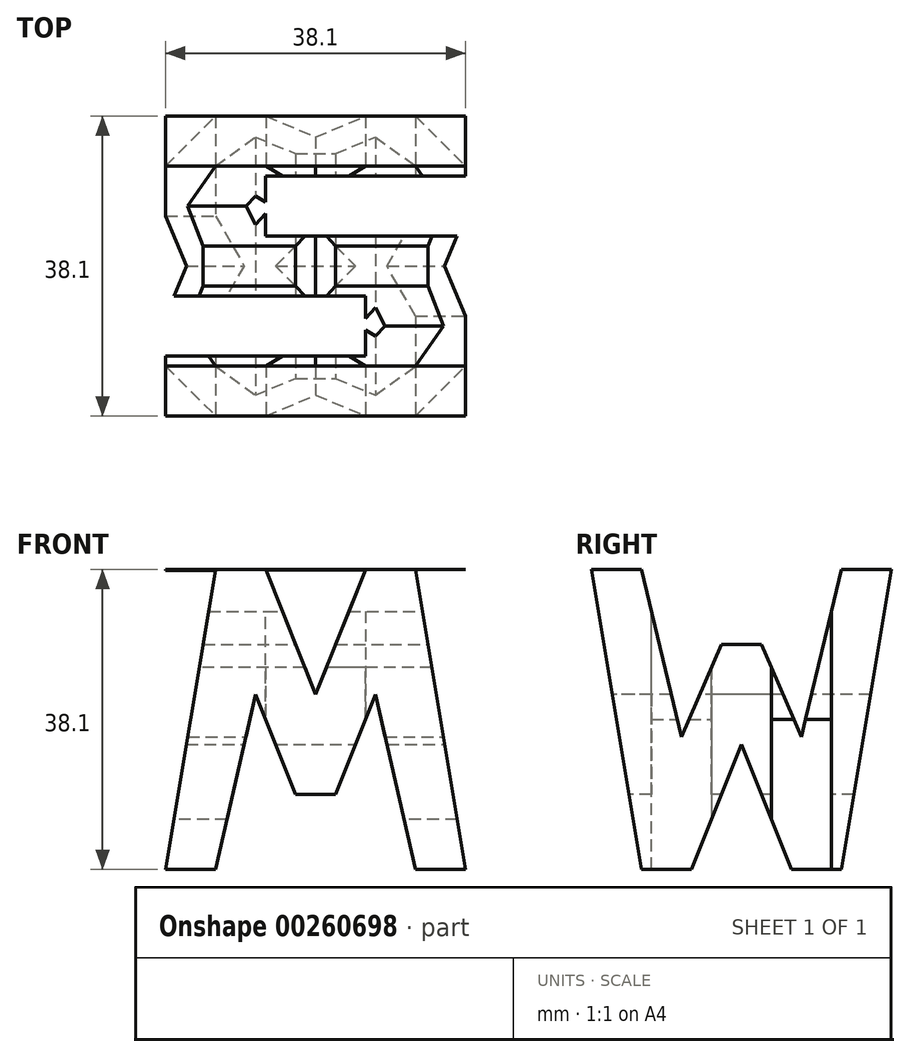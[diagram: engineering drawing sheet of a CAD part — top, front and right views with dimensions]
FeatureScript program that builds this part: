
annotation { "Feature Type Name" : "Feature", "Feature Type Description" : "" }
export const myFeature = defineFeature(function(context is Context, id is Id, definition is map)
    precondition{}
    {
        {
            var Q0;
            Q0=qCreatedBy(makeId("Front.planeOp"),FACE);
            var sketch = newSketch(context, id + "F0", { "sketchPlane" : qUnion([Q0])});
            skLineSegment(sketch, "E0", {"start": v(0, 0) * mm, "end": v(0, 38.1) * mm});
            skLineSegment(sketch, "E1", {"start": v(0, 38.1) * mm, "end": v(38.1, 38.1) * mm});
            skLineSegment(sketch, "E2", {"start": v(38.1, 38.1) * mm, "end": v(38.1, 0) * mm});
            skLineSegment(sketch, "E3", {"start": v(38.1, 0) * mm, "end": v(0, 0) * mm});
            skSolve(sketch);
        }
        {
            var Q0;
            Q0=makeQuery(id+"F0.imprint","IMPRINT",FACE,{"disambiguationData":[TD([[makeQuery(id+"F0.imprint","IMPRINT",EDGE,{"derivedFrom":sQuery(id+"F0.wireOp",EDGE,"E0")}),-1.0]])]});
            extrude(context, id + "F1", {"entities" : qUnion([Q0]), "depth" : 38.1 * mm});
        }
        {
            var Q0;
            Q0=qCreatedBy(makeId("Front.planeOp"),FACE);
            cPlane(context, id + "F2", {"entities" : qUnion([Q0]), "cplaneType" : CPlaneType.OFFSET, "offset" : 38.1 * mm, "width" : 152.4 * mm, "height" : 152.4 * mm});
        }
        {
            var Q0;
            Q0=qCreatedBy(makeId("Right.planeOp"),FACE);
            cPlane(context, id + "F3", {"entities" : qUnion([Q0]), "cplaneType" : CPlaneType.OFFSET, "offset" : 38.1 * mm, "width" : 152.4 * mm, "height" : 152.4 * mm});
        }
        {
            var Q0;
            Q0=qCreatedBy(makeId("Top.planeOp"),FACE);
            cPlane(context, id + "F4", {"entities" : qUnion([Q0]), "cplaneType" : CPlaneType.OFFSET, "offset" : 38.1 * mm, "width" : 152.4 * mm, "height" : 152.4 * mm});
        }
        {
            var Q0;
            Q0=qCreatedBy(id+"F3.planeOp",FACE);
            var sketch = newSketch(context, id + "F5", { "sketchPlane" : qUnion([Q0])});
            skLineSegment(sketch, "E4", {"start": v(-38.1, 38.1) * mm, "end": v(-31.75, 0) * mm});
            skLineSegment(sketch, "E5", {"start": v(-31.75, 38.1) * mm, "end": v(-26.67, 16.82) * mm});
            skLineSegment(sketch, "E6", {"start": v(-26.67, 16.82) * mm, "end": v(-21.59, 28.58) * mm});
            skLineSegment(sketch, "E7", {"start": v(-21.59, 28.58) * mm, "end": v(-16.5, 28.58) * mm});
            skLineSegment(sketch, "E8", {"start": v(-16.5, 28.58) * mm, "end": v(-11.43, 16.82) * mm});
            skLineSegment(sketch, "E9", {"start": v(-11.43, 16.82) * mm, "end": v(-6.35, 38.1) * mm});
            skLineSegment(sketch, "E10", {"start": v(-38.1, 38.1) * mm, "end": v(-31.75, 38.1) * mm});
            skLineSegment(sketch, "E11", {"start": v(-6.35, 38.1) * mm, "end": v(0, 38.1) * mm});
            skLineSegment(sketch, "E12", {"start": v(-38.1, 38.1) * mm, "end": v(-38.1, 0) * mm});
            skLineSegment(sketch, "E13", {"start": v(-38.1, 0) * mm, "end": v(0, 0) * mm});
            skLineSegment(sketch, "E14", {"start": v(0, 0) * mm, "end": v(0, 38.1) * mm});
            skLineSegment(sketch, "E15", {"start": v(0, 38.1) * mm, "end": v(-38.1, 38.1) * mm});
            skLineSegment(sketch, "E16", {"start": v(-31.75, 0) * mm, "end": v(-22.93, 0) * mm});
            skLineSegment(sketch, "E17", {"start": v(-30.58, 0) * mm, "end": v(-19.05, 0) * mm});
            skLineSegment(sketch, "E18", {"start": v(0, 38.1) * mm, "end": v(-6.35, 0) * mm});
            skLineSegment(sketch, "E19", {"start": v(-25.4, 0) * mm, "end": v(-19.05, 15.88) * mm});
            skLineSegment(sketch, "E20", {"start": v(-19.05, 15.88) * mm, "end": v(-12.7, 0) * mm});
            skSolve(sketch);
        }
        {
            var Q0;
            {var subQ0=sQuery(id+"F5.wireOp",EDGE,"E5");Q0=makeQuery(id+"F5.imprint","IMPRINT",FACE,{"disambiguationData":[TD([[makeQuery(id+"F5.imprint","IMPRINT",EDGE,{"derivedFrom":subQ0}),1.0]])]});}
            var Q1;
            {var subQ0=sQuery(id+"F5.wireOp",EDGE,"E4");Q1=makeQuery(id+"F5.imprint","IMPRINT",FACE,{"disambiguationData":[TD([[makeQuery(id+"F5.imprint","IMPRINT",EDGE,{"derivedFrom":subQ0}),-1.0]])]});}
            var Q2;
            {var subQ4=sQuery(id+"F5.wireOp",EDGE,"E19");Q2=makeQuery(id+"F5.imprint","IMPRINT",FACE,{"disambiguationData":[TD([[makeQuery(id+"F5.imprint","IMPRINT",EDGE,{"derivedFrom":subQ4}),-1.0]])]});}
            var Q3;
            {var subQ0=sQuery(id+"F5.wireOp",EDGE,"E14");Q3=makeQuery(id+"F5.imprint","IMPRINT",FACE,{"disambiguationData":[TD([[makeQuery(id+"F5.imprint","IMPRINT",EDGE,{"derivedFrom":subQ0}),1.0]])]});}
            extrude(context, id + "F6", {"entities" : qUnion([Q0, Q1, Q2, Q3]), "operationType" : NewBodyOperationType.REMOVE, "oppositeDirection" : true, "depth" : 38.1 * mm});
        }
        {
            var Q0;
            Q0=qCreatedBy(id+"F2.planeOp",FACE);
            var sketch = newSketch(context, id + "F7", { "sketchPlane" : qUnion([Q0])});
            skLineSegment(sketch, "E21", {"start": v(0, 37.97) * mm, "end": v(0, 0) * mm});
            skLineSegment(sketch, "E22", {"start": v(0, 0) * mm, "end": v(38.1, 0) * mm});
            skLineSegment(sketch, "E23", {"start": v(38.1, 0) * mm, "end": v(38.1, 38.1) * mm});
            skLineSegment(sketch, "E24", {"start": v(38.1, 38.1) * mm, "end": v(0, 37.97) * mm});
            skSolve(sketch);
        }
        {
            var Q0;
            Q0=makeQuery(id+"F7.imprint","IMPRINT",FACE,{"disambiguationData":[TD([[makeQuery(id+"F7.imprint","IMPRINT",EDGE,{"derivedFrom":sQuery(id+"F7.wireOp",EDGE,"E21")}),1.0]])]});
            var sketch = newSketch(context, id + "F8", { "sketchPlane" : qUnion([Q0])});
            skLineSegment(sketch, "E25", {"start": v(0, 0) * mm, "end": v(6.35, 38.1) * mm});
            skLineSegment(sketch, "E26", {"start": v(12.7, 38.1) * mm, "end": v(19.05, 22.23) * mm});
            skLineSegment(sketch, "E27", {"start": v(19.05, 22.23) * mm, "end": v(25.4, 38.1) * mm});
            skLineSegment(sketch, "E28", {"start": v(31.75, 38.1) * mm, "end": v(38.1, 0) * mm});
            skLineSegment(sketch, "E29", {"start": v(6.35, 0) * mm, "end": v(11.43, 22.22) * mm});
            skLineSegment(sketch, "E30", {"start": v(11.43, 22.22) * mm, "end": v(16.51, 9.52) * mm});
            skLineSegment(sketch, "E31", {"start": v(16.51, 9.53) * mm, "end": v(21.59, 9.53) * mm});
            skLineSegment(sketch, "E32", {"start": v(21.59, 9.52) * mm, "end": v(26.67, 22.22) * mm});
            skLineSegment(sketch, "E33", {"start": v(26.67, 22.22) * mm, "end": v(31.75, 0) * mm});
            skLineSegment(sketch, "E34", {"start": v(0, 38.1) * mm, "end": v(0, 0) * mm});
            skLineSegment(sketch, "E35", {"start": v(38.1, 0) * mm, "end": v(38.1, 38.1) * mm});
            skLineSegment(sketch, "E36", {"start": v(38.1, 38.1) * mm, "end": v(0, 38.1) * mm});
            skLineSegment(sketch, "E37", {"start": v(0, 38.1) * mm, "end": v(38.1, 38.1) * mm});
            skLineSegment(sketch, "E38", {"start": v(0, 0) * mm, "end": v(38.1, 0) * mm});
            skLineSegment(sketch, "E39", {"start": v(38.1, 0) * mm, "end": v(0, 0) * mm});
            skSolve(sketch);
        }
        {
            var Q0;
            {var subQ0=sQuery(id+"F8.wireOp",EDGE,"E34");var subQ3=makeQuery(id+"F7.imprint","IMPRINT",EDGE,{"derivedFrom":sQuery(id+"F7.wireOp",EDGE,"E24")});var subQ5=makeQuery(id+"F8.imprint","INTERSECT",VERTEX,{"derivedFrom":[subQ3,subQ0]});Q0=makeQuery(id+"F8.imprint","IMPRINT",FACE,{"disambiguationData":[TD([[makeQuery(id+"F8.imprint","IMPRINT",EDGE,{"disambiguationData":[TD([[subQ5,1.0]])],"derivedFrom":subQ3}),1.0]])]});}
            var Q1;
            {var subQ0=sQuery(id+"F8.wireOp",EDGE,"E29");Q1=makeQuery(id+"F8.imprint","IMPRINT",FACE,{"disambiguationData":[TD([[makeQuery(id+"F8.imprint","IMPRINT",EDGE,{"derivedFrom":subQ0}),-1.0]])]});}
            var Q2;
            {var subQ0=sQuery(id+"F8.wireOp",EDGE,"E35");Q2=makeQuery(id+"F8.imprint","IMPRINT",FACE,{"disambiguationData":[TD([[makeQuery(id+"F8.imprint","IMPRINT",EDGE,{"derivedFrom":subQ0}),1.0]])]});}
            var Q3;
            {var subQ0=sQuery(id+"F8.wireOp",EDGE,"E27");var subQ1=sQuery(id+"F8.wireOp",EDGE,"E26");var subQ2=makeQuery(id+"F8.imprint","INTERSECT",VERTEX,{"derivedFrom":[subQ1,subQ0]});Q3=makeQuery(id+"F8.imprint","IMPRINT",FACE,{"disambiguationData":[TD([[makeQuery(id+"F8.imprint","IMPRINT",EDGE,{"disambiguationData":[TD([[subQ2,1.0]])],"derivedFrom":subQ1}),1.0]])]});}
            extrude(context, id + "F9", {"entities" : qUnion([Q0, Q1, Q2, Q3]), "operationType" : NewBodyOperationType.REMOVE, "oppositeDirection" : true, "depth" : 38.1 * mm});
        }
        {
            var Q0;
            Q0=qCreatedBy(id+"F4.planeOp",FACE);
            var sketch = newSketch(context, id + "F10", { "sketchPlane" : qUnion([Q0])});
            skLineSegment(sketch, "E40", {"start": v(0, 0) * mm, "end": v(0, -38.1) * mm});
            skLineSegment(sketch, "E41", {"start": v(0, -38.1) * mm, "end": v(38.1, -38.1) * mm});
            skLineSegment(sketch, "E42", {"start": v(38.1, -38.1) * mm, "end": v(38.1, 0) * mm});
            skLineSegment(sketch, "E43", {"start": v(38.1, 0) * mm, "end": v(0, 0) * mm});
            skLineSegment(sketch, "E44", {"start": v(38.1, -7.62) * mm, "end": v(12.7, -7.62) * mm});
            skLineSegment(sketch, "E45", {"start": v(12.7, -7.62) * mm, "end": v(12.7, -15.24) * mm});
            skLineSegment(sketch, "E46", {"start": v(12.7, -15.24) * mm, "end": v(38.1, -15.24) * mm});
            skLineSegment(sketch, "E47", {"start": v(0, -22.86) * mm, "end": v(25.4, -22.86) * mm});
            skLineSegment(sketch, "E48", {"start": v(25.4, -22.86) * mm, "end": v(25.4, -30.48) * mm});
            skLineSegment(sketch, "E49", {"start": v(25.4, -30.48) * mm, "end": v(0, -30.48) * mm});
            skSolve(sketch);
        }
        {
            var Q0;
            {var subQ0=sQuery(id+"F10.wireOp",EDGE,"E44");Q0=makeQuery(id+"F10.imprint","IMPRINT",FACE,{"disambiguationData":[TD([[makeQuery(id+"F10.imprint","IMPRINT",EDGE,{"derivedFrom":subQ0}),1.0]])]});}
            var Q1;
            {var subQ0=sQuery(id+"F10.wireOp",EDGE,"E47");Q1=makeQuery(id+"F10.imprint","IMPRINT",FACE,{"disambiguationData":[TD([[makeQuery(id+"F10.imprint","IMPRINT",EDGE,{"derivedFrom":subQ0}),-1.0]])]});}
            extrude(context, id + "F11", {"entities" : qUnion([Q0, Q1]), "operationType" : NewBodyOperationType.REMOVE, "oppositeDirection" : true, "depth" : 38.1 * mm});
        }
    });
